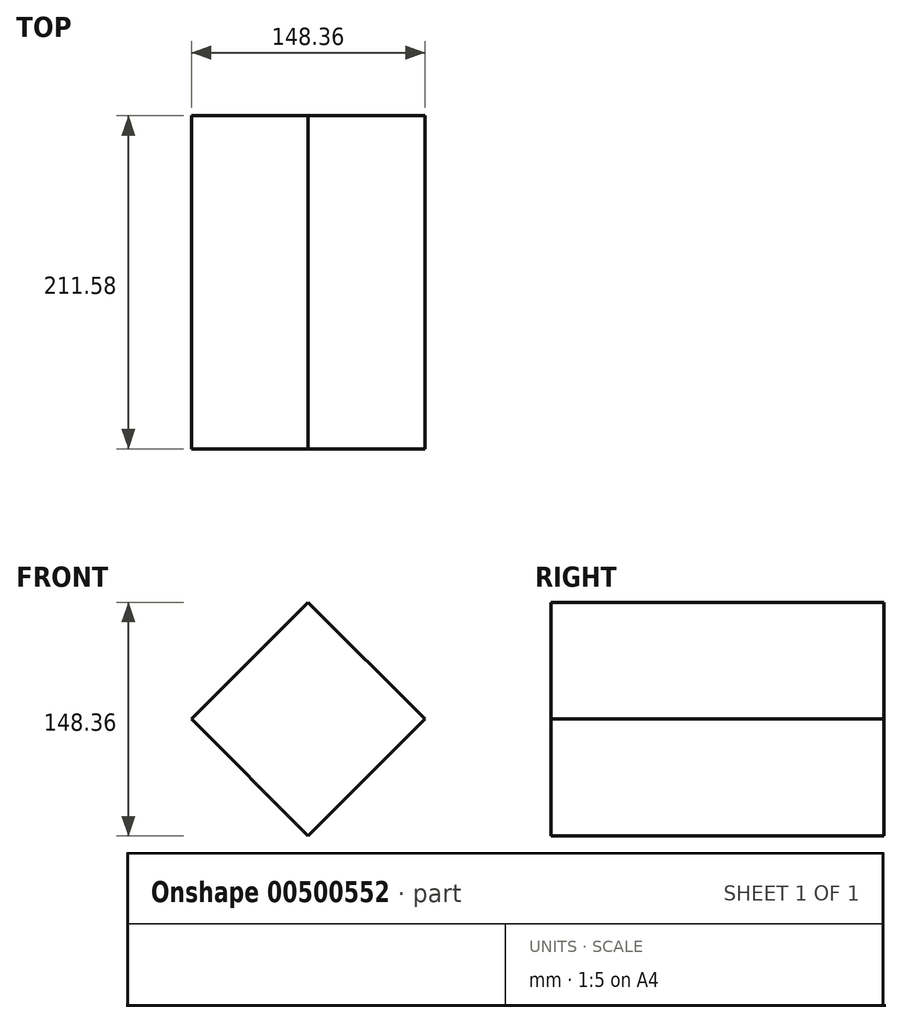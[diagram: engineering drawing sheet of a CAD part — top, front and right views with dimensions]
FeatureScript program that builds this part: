
annotation { "Feature Type Name" : "Feature", "Feature Type Description" : "" }
export const myFeature = defineFeature(function(context is Context, id is Id, definition is map)
    precondition{}
    {
        {
            var Q0;
            Q0=qCreatedBy(makeId("Front.planeOp"),FACE);
            var sketch = newSketch(context, id + "F0", { "sketchPlane" : qUnion([Q0])});
            skCircle(sketch, "E0.cCircle", {"center": v(0, 0) * mm, "radius": 74.18 * mm, "construction": true});
            skLineSegment(sketch, "E0.0", {"start": v(0, 74.18) * mm, "end": v(74.18, 0) * mm});
            skLineSegment(sketch, "E0.1", {"start": v(74.18, 0) * mm, "end": v(0, -74.18) * mm});
            skLineSegment(sketch, "E0.2", {"start": v(0, -74.18) * mm, "end": v(-74.18, 0) * mm});
            skLineSegment(sketch, "E0.3", {"start": v(-74.18, 0) * mm, "end": v(0, 74.18) * mm});
            skSolve(sketch);
        }
        {
            var Q0;
            Q0=makeQuery(id+"F0.imprint","IMPRINT",FACE,{"disambiguationData":[TD([[makeQuery(id+"F0.imprint","IMPRINT",EDGE,{"derivedFrom":sQuery(id+"F0.wireOp",EDGE,"E0.0")}),-1.0]])]});
            extrude(context, id + "F1", {"entities" : qUnion([Q0]), "depth" : 211.58 * mm});
        }
    });
